annotation { "Feature Type Name" : "Feature", "Feature Type Description" : "" }
export const myFeature = defineFeature(function(context is Context, id is Id, definition is map)
    precondition{}
    {
        {
            var Q0;
            Q0=qCreatedBy(makeId("Top.planeOp"),FACE);
            var sketch = newSketch(context, id + "F0", { "sketchPlane" : qUnion([Q0])});
            skLineSegment(sketch, "E0.bottom", {"start": v(-4.39, 19.99) * mm, "end": v(107.61, 19.99) * mm});
            skLineSegment(sketch, "E0.top", {"start": v(-4.39, -4.01) * mm, "end": v(107.61, -4.01) * mm});
            skLineSegment(sketch, "E0.left", {"start": v(-4.39, 19.99) * mm, "end": v(-4.39, -4.01) * mm});
            skLineSegment(sketch, "E0.right", {"start": v(107.61, 19.99) * mm, "end": v(107.61, -4.01) * mm});
            skSolve(sketch);
        }
        {
            var Q0;
            Q0 = qSketchRegion(id + "F0", true);
            extrude(context, id + "F1", {"entities" : qUnion([Q0]), "depth" : 80 * mm});
        }
        {
            var Q0;
            Q0=makeQuery(id+"F1.opExtrude","CAP_FACE",FACE,{"disambiguationData":[OSD([sQuery(id+"F0.wireOp",EDGE,"E0.bottom"),sQuery(id+"F0.wireOp",EDGE,"E0.top"),sQuery(id+"F0.wireOp",EDGE,"E0.left"),sQuery(id+"F0.wireOp",EDGE,"E0.right")])],"isStart":false});
            var sketch = newSketch(context, id + "F2", { "sketchPlane" : qUnion([Q0])});
            skLineSegment(sketch, "E1.bottom", {"start": v(-0.39, 15.99) * mm, "end": v(103.61, 15.99) * mm});
            skLineSegment(sketch, "E1.top", {"start": v(-0.39, -0.01) * mm, "end": v(103.61, -0.01) * mm});
            skLineSegment(sketch, "E1.left", {"start": v(-0.39, 15.99) * mm, "end": v(-0.39, -0.01) * mm});
            skLineSegment(sketch, "E1.right", {"start": v(103.61, 15.99) * mm, "end": v(103.61, -0.01) * mm});
            skSolve(sketch);
        }
        {
            var Q0;
            Q0 = qSketchRegion(id + "F2", true);
            extrude(context, id + "F3", {"entities" : qUnion([Q0]), "operationType" : NewBodyOperationType.REMOVE, "oppositeDirection" : true, "depth" : 78 * mm});
        }
        {
            var Q0;
            Q0=makeQuery(id+"F1.opExtrude","CAP_FACE",FACE,{"disambiguationData":[OSD([sQuery(id+"F0.wireOp",EDGE,"E0.bottom"),sQuery(id+"F0.wireOp",EDGE,"E0.top"),sQuery(id+"F0.wireOp",EDGE,"E0.left"),sQuery(id+"F0.wireOp",EDGE,"E0.right")])],"isStart":false});
            var sketch = newSketch(context, id + "F4", { "sketchPlane" : qUnion([Q0])});
            skLineSegment(sketch, "E2", {"start": v(-2.39, 17.99) * mm, "end": v(105.61, 17.99) * mm});
            skLineSegment(sketch, "E3", {"start": v(105.61, 17.99) * mm, "end": v(105.61, -2.01) * mm});
            skLineSegment(sketch, "E4", {"start": v(105.61, -2.01) * mm, "end": v(-2.39, -2.01) * mm});
            skLineSegment(sketch, "E5", {"start": v(-2.39, -2.01) * mm, "end": v(-2.39, 17.99) * mm});
            skSolve(sketch);
        }
        {
            var Q0;
            Q0=makeQuery(id+"F4.imprint","IMPRINT",FACE,{"disambiguationData":[TD([[makeQuery(id+"F4.imprint","IMPRINT",EDGE,{"derivedFrom":sQuery(id+"F4.wireOp",EDGE,"E2")}),1.0]])]});
            extrude(context, id + "F5", {"entities" : qUnion([Q0]), "operationType" : NewBodyOperationType.REMOVE, "oppositeDirection" : true, "depth" : 10 * mm});
        }
        {
            var Q0;
            Q0=makeQuery(id+"F1.opExtrude","SWEPT_FACE",FACE,{"disambiguationData":[OSD([sQuery(id+"F0.wireOp",EDGE,"E0.top")])]});
            var sketch = newSketch(context, id + "F6", { "sketchPlane" : qUnion([Q0])});
            skText(sketch, "E6", { "text": "Lithophane Photos", "fontName": "OpenSans-Bold.ttf"});
            const initialGuessF6  = {"E6": [0.004, 0.03724, 1, 0, 0.00714]};
            skSetInitialGuess(sketch, initialGuessF6);
            skSolve(sketch);
        }
        {
            var Q0;
            Q0 = qSketchRegion(id + "F6", true);
            extrude(context, id + "F7", {"entities" : qUnion([Q0]), "operationType" : NewBodyOperationType.REMOVE, "oppositeDirection" : true, "depth" : 2 * mm});
        }
    });